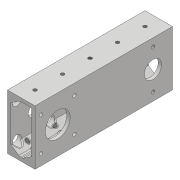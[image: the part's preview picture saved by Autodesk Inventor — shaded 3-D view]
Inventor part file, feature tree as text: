
AUTODESK INVENTOR PART (.ipt)
format: ipt  version: 2018 (Build 220112000, 112)  size: 1,001,472 bytes
history: native  units: mm
features: sketch x7, hole x5, extrude x3, chamfer x3, fillet x3, other x3, shell x1, pattern_linear x1, mirror x1, reference x1, projected_geometry x1
ambient origin geometry x8: Origin, YZ Plane, XZ Plane, XY Plane, X Axis, Y Axis, Z Axis, Center Point
bodies: Solid1 (feature_tree)
feature tree (29):
  extrude  "Extrusion1"  Depth=25.4mm
  shell  "Shell1"  Thickness=127.0mm
  chamfer  "Chamfer1"  Distance=23.0mm
  chamfer  "Chamfer2"  Distance=50.8mm
  chamfer  "Chamfer3"  Distance=16.0mm
  sketch  "Sketch2"  dims[d4=3.175mm]
  hole  "Hole1"  [1 undecoded]
  hole  "Hole2"  [1 undecoded]
  extrude  "Extrusion2"  Depth=36.0mm
  extrude  "Extrusion3"  Depth=50.8mm
  hole  "Hole4"  [1 undecoded]
  hole  "Hole5"  [1 undecoded]
  fillet  "Fillet3"  Radius=8.0mm
  pattern_linear  "Rectangular Pattern1"  Spacing1=1.5mm  [1 undecoded]
  mirror  "Mirror1"
  hole  "Hole6"  [1 undecoded]
  fillet  "Fillet4"  Radius=38.1mm
  fillet  "Fillet5"  Radius=14.0mm
  sketch  "Sketch1"  dims[d0=50.8mm d1=25.4mm d2=127.0mm d3=0.0mm]
  sketch  "Sketch3"  dims[d5=31.0mm]
  sketch  "Sketch4"  dims[d6=31.0mm]
  sketch  "Sketch6"  dims[d7=21.0mm]
  sketch  "Sketch7"  dims[d8=3.2mm d9=6.0mm d10=8.0mm d11=22.225mm d12=90.0deg d13=8.0mm d14=20.594885mm]
  reference  "Reference1"
  sketch  "Sketch8"  dims[d15=10.0mm d16=6.0mm d17=6.5mm d18=3.0mm d19=90.0deg d20=8.0mm d21=20.594885mm d22=23.0mm d23=50.8mm d24=0.0mm d25=16.0mm d26=18.0mm d27=50.8mm d28=0.0mm d40=3.242mm d41=100.0mm d42=6.5mm d43=3.0mm d44=90.0deg d45=11.8mm d46=20.594885mm d47=36.0mm d48=3.242mm d49=100.0mm d50=6.5mm d51=3.0mm d52=90.0deg d53=11.8mm d54=20.594885mm d55=50.8mm d56=8.0mm d57=5.5mm d58=45.0deg d59=5.5mm d60=8.0mm d61=45.0deg d62=8.0mm d63=5.5mm d64=45.0deg d70=1.5mm d72=20.0mm d74=50.8mm d75=38.1mm d76=14.0mm d77=3.242mm d78=8.0mm d79=4.0mm d80=2.0mm d81=90.0deg d82=11.8mm d83=20.594885mm d84=3.0mm d85=0.5mm]
  projected_geometry  "Projected Loop1"
  parser-record x1  (decoder bookkeeping rows leaked as tree rows — omitted from the tree; the rows remain in map.json)
  other  "AMR_Transm2.iam"
  other  "7804K147_STAINLESS STEEL BALL BEARING:2"
note: 6 required parameter values undecoded (feature->parameter linkage not recoverable at this tier; creation-order binding heuristic only, values carry confidence <= 0.55)
note: 1 file-system path scrubbed to <path> (originals preserved in map.json)
